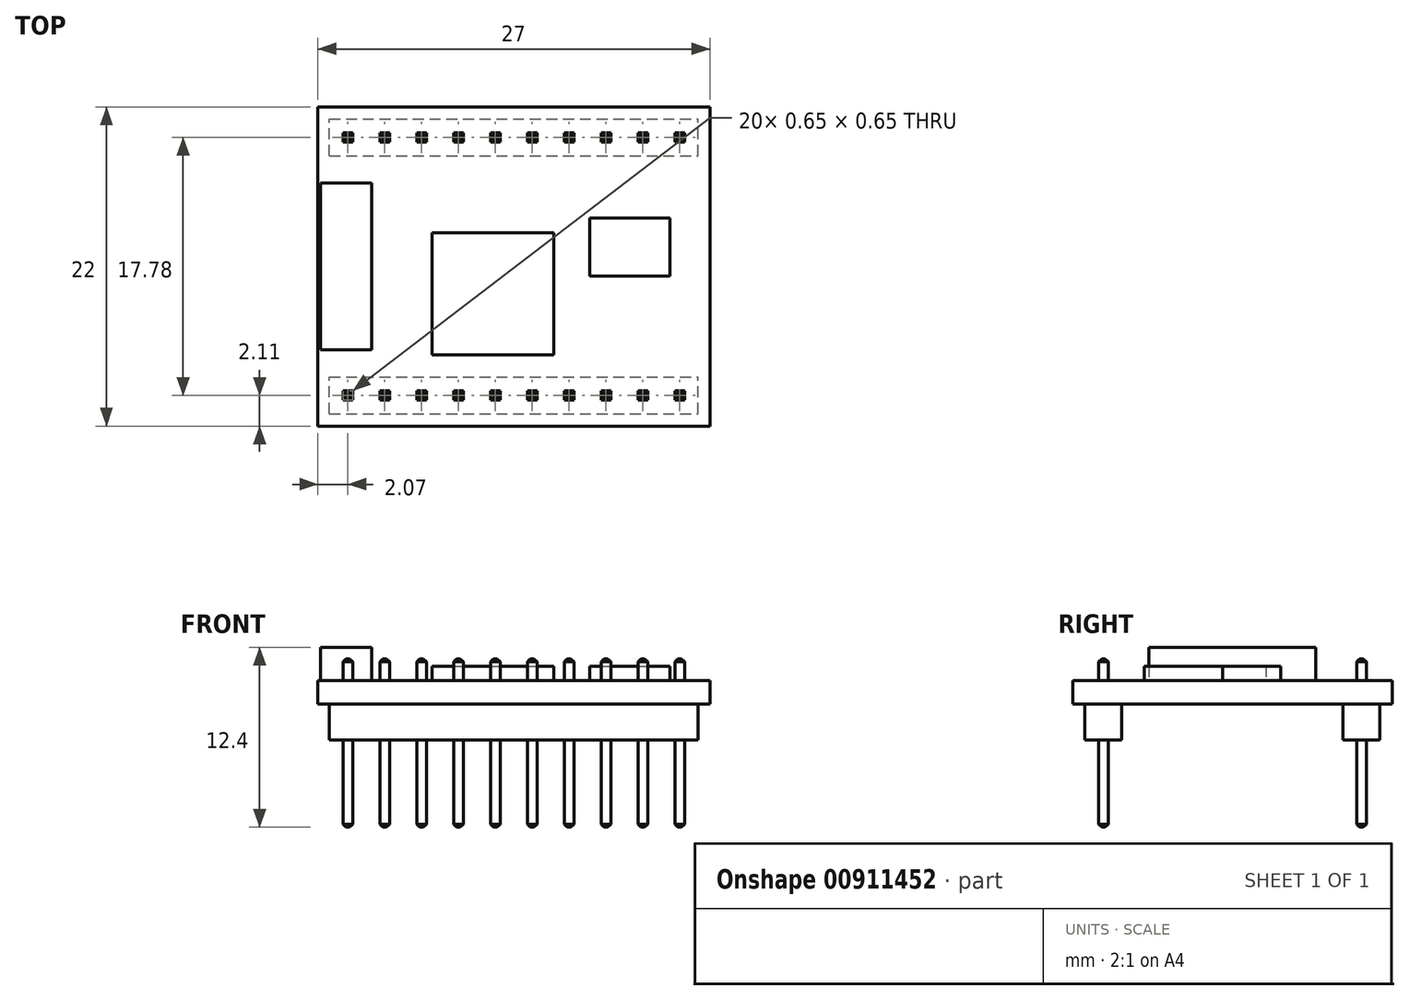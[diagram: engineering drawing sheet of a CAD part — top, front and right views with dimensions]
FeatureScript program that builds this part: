
annotation { "Feature Type Name" : "Feature", "Feature Type Description" : "" }
export const myFeature = defineFeature(function(context is Context, id is Id, definition is map)
    precondition{}
    {
        {
            var Q0;
            Q0=qCreatedBy(makeId("Top.planeOp"),FACE);
            var sketch = newSketch(context, id + "F0", { "sketchPlane" : qUnion([Q0])});
            skLineSegment(sketch, "E0.bottom", {"start": v(-13.5, -11) * mm, "end": v(13.5, -11) * mm});
            skLineSegment(sketch, "E0.top", {"start": v(-13.5, 11) * mm, "end": v(13.5, 11) * mm});
            skLineSegment(sketch, "E0.left", {"start": v(-13.5, -11) * mm, "end": v(-13.5, 11) * mm});
            skLineSegment(sketch, "E0.right", {"start": v(13.5, -11) * mm, "end": v(13.5, 11) * mm});
            skLineSegment(sketch, "E1", {"start": v(-13.5, 11) * mm, "end": v(0, 0) * mm, "construction": true});
            skLineSegment(sketch, "E2", {"start": v(0, 0) * mm, "end": v(-13.5, -11) * mm, "construction": true});
            skLineSegment(sketch, "E3", {"start": v(0, 0) * mm, "end": v(13.5, 11) * mm, "construction": true});
            skSolve(sketch);
        }
        {
            var Q0;
            Q0 = qSketchRegion(id + "F0", true);
            extrude(context, id + "F1", {"entities" : qUnion([Q0]), "depth" : 1.6 * mm, "offsetDistance" : 25 * mm});
        }
        {
            var Q0;
            Q0=makeQuery(id+"F1.opExtrude","CAP_FACE",FACE,{"disambiguationData":[OSD([sQuery(id+"F0.wireOp",EDGE,"E0.bottom"),sQuery(id+"F0.wireOp",EDGE,"E0.top"),sQuery(id+"F0.wireOp",EDGE,"E0.left"),sQuery(id+"F0.wireOp",EDGE,"E0.right")])],"isStart":true});
            var sketch = newSketch(context, id + "F2", { "sketchPlane" : qUnion([Q0])});
            skLineSegment(sketch, "E4.bottom", {"start": v(-12.7, 10.16) * mm, "end": v(12.7, 10.16) * mm});
            skLineSegment(sketch, "E4.top", {"start": v(-12.7, 7.62) * mm, "end": v(12.7, 7.62) * mm});
            skLineSegment(sketch, "E4.left", {"start": v(-12.7, 10.16) * mm, "end": v(-12.7, 7.62) * mm});
            skLineSegment(sketch, "E4.right", {"start": v(12.7, 10.16) * mm, "end": v(12.7, 7.62) * mm});
            skLineSegment(sketch, "E5.bottom", {"start": v(-12.7, -7.62) * mm, "end": v(12.7, -7.62) * mm});
            skLineSegment(sketch, "E5.top", {"start": v(-12.7, -10.16) * mm, "end": v(12.7, -10.16) * mm});
            skLineSegment(sketch, "E5.left", {"start": v(-12.7, -7.62) * mm, "end": v(-12.7, -10.16) * mm});
            skLineSegment(sketch, "E5.right", {"start": v(12.7, -7.62) * mm, "end": v(12.7, -10.16) * mm});
            skLineSegment(sketch, "E6", {"start": v(-13.5, 11) * mm, "end": v(-12.7, 10.16) * mm, "construction": true});
            skLineSegment(sketch, "E7", {"start": v(12.7, 10.16) * mm, "end": v(13.5, 11) * mm, "construction": true});
            skLineSegment(sketch, "E8", {"start": v(-12.7, -10.16) * mm, "end": v(-13.5, -11) * mm, "construction": true});
            skSolve(sketch);
        }
        {
            var Q0;
            Q0 = qSketchRegion(id + "F2", true);
            extrude(context, id + "F3", {"entities" : qUnion([Q0]), "operationType" : NewBodyOperationType.ADD, "depth" : 2.5 * mm, "offsetDistance" : 25 * mm});
        }
        {
            var Q0;
            Q0=makeQuery(id+"F3.opExtrude","CAP_FACE",FACE,{"disambiguationData":[OSD([sQuery(id+"F2.wireOp",EDGE,"E4.bottom"),sQuery(id+"F2.wireOp",EDGE,"E4.top"),sQuery(id+"F2.wireOp",EDGE,"E4.left"),sQuery(id+"F2.wireOp",EDGE,"E4.right")])],"isStart":false});
            var sketch = newSketch(context, id + "F4", { "sketchPlane" : qUnion([Q0])});
            skLineSegment(sketch, "E9.bottom", {"start": v(-11.75, 9.22) * mm, "end": v(-11.1, 9.22) * mm});
            skLineSegment(sketch, "E9.top", {"start": v(-11.75, 8.56) * mm, "end": v(-11.1, 8.56) * mm});
            skLineSegment(sketch, "E9.left", {"start": v(-11.75, 9.22) * mm, "end": v(-11.75, 8.56) * mm});
            skLineSegment(sketch, "E9.right", {"start": v(-11.1, 9.22) * mm, "end": v(-11.1, 8.56) * mm});
            skLineSegment(sketch, "E10.1.0.0", {"start": v(-8.56, 9.22) * mm, "end": v(-8.56, 8.56) * mm});
            skLineSegment(sketch, "E10.1.0.1", {"start": v(-9.21, 8.56) * mm, "end": v(-8.56, 8.56) * mm});
            skLineSegment(sketch, "E10.1.0.2", {"start": v(-9.21, 9.22) * mm, "end": v(-9.21, 8.56) * mm});
            skLineSegment(sketch, "E10.1.0.3", {"start": v(-9.21, 9.22) * mm, "end": v(-8.56, 9.22) * mm});
            skLineSegment(sketch, "E10.2.0.0", {"start": v(-6.02, 9.22) * mm, "end": v(-6.02, 8.56) * mm});
            skLineSegment(sketch, "E10.2.0.1", {"start": v(-6.67, 8.56) * mm, "end": v(-6.02, 8.56) * mm});
            skLineSegment(sketch, "E10.2.0.2", {"start": v(-6.67, 9.22) * mm, "end": v(-6.67, 8.56) * mm});
            skLineSegment(sketch, "E10.2.0.3", {"start": v(-6.67, 9.22) * mm, "end": v(-6.02, 9.22) * mm});
            skLineSegment(sketch, "E10.3.0.0", {"start": v(-3.48, 9.22) * mm, "end": v(-3.48, 8.56) * mm});
            skLineSegment(sketch, "E10.3.0.1", {"start": v(-4.13, 8.56) * mm, "end": v(-3.48, 8.56) * mm});
            skLineSegment(sketch, "E10.3.0.2", {"start": v(-4.13, 9.22) * mm, "end": v(-4.13, 8.56) * mm});
            skLineSegment(sketch, "E10.3.0.3", {"start": v(-4.13, 9.22) * mm, "end": v(-3.48, 9.22) * mm});
            skLineSegment(sketch, "E10.4.0.0", {"start": v(-0.94, 9.22) * mm, "end": v(-0.94, 8.56) * mm});
            skLineSegment(sketch, "E10.4.0.1", {"start": v(-1.6, 8.56) * mm, "end": v(-0.94, 8.56) * mm});
            skLineSegment(sketch, "E10.4.0.2", {"start": v(-1.6, 9.22) * mm, "end": v(-1.6, 8.56) * mm});
            skLineSegment(sketch, "E10.4.0.3", {"start": v(-1.6, 9.22) * mm, "end": v(-0.94, 9.22) * mm});
            skLineSegment(sketch, "E10.5.0.0", {"start": v(1.6, 9.22) * mm, "end": v(1.6, 8.56) * mm});
            skLineSegment(sketch, "E10.5.0.1", {"start": v(0.95, 8.56) * mm, "end": v(1.6, 8.56) * mm});
            skLineSegment(sketch, "E10.5.0.2", {"start": v(0.95, 9.22) * mm, "end": v(0.95, 8.56) * mm});
            skLineSegment(sketch, "E10.5.0.3", {"start": v(0.95, 9.22) * mm, "end": v(1.6, 9.22) * mm});
            skLineSegment(sketch, "E10.6.0.0", {"start": v(4.14, 9.22) * mm, "end": v(4.14, 8.56) * mm});
            skLineSegment(sketch, "E10.6.0.1", {"start": v(3.49, 8.56) * mm, "end": v(4.14, 8.56) * mm});
            skLineSegment(sketch, "E10.6.0.2", {"start": v(3.49, 9.22) * mm, "end": v(3.49, 8.56) * mm});
            skLineSegment(sketch, "E10.6.0.3", {"start": v(3.49, 9.22) * mm, "end": v(4.14, 9.22) * mm});
            skLineSegment(sketch, "E10.7.0.0", {"start": v(6.68, 9.22) * mm, "end": v(6.68, 8.56) * mm});
            skLineSegment(sketch, "E10.7.0.1", {"start": v(6.03, 8.56) * mm, "end": v(6.68, 8.56) * mm});
            skLineSegment(sketch, "E10.7.0.2", {"start": v(6.03, 9.22) * mm, "end": v(6.03, 8.56) * mm});
            skLineSegment(sketch, "E10.7.0.3", {"start": v(6.03, 9.22) * mm, "end": v(6.68, 9.22) * mm});
            skLineSegment(sketch, "E10.8.0.0", {"start": v(9.22, 9.22) * mm, "end": v(9.22, 8.56) * mm});
            skLineSegment(sketch, "E10.8.0.1", {"start": v(8.57, 8.56) * mm, "end": v(9.22, 8.56) * mm});
            skLineSegment(sketch, "E10.8.0.2", {"start": v(8.57, 9.22) * mm, "end": v(8.57, 8.56) * mm});
            skLineSegment(sketch, "E10.8.0.3", {"start": v(8.57, 9.22) * mm, "end": v(9.22, 9.22) * mm});
            skLineSegment(sketch, "E10.9.0.0", {"start": v(11.76, 9.22) * mm, "end": v(11.76, 8.56) * mm});
            skLineSegment(sketch, "E10.9.0.1", {"start": v(11.1, 8.56) * mm, "end": v(11.76, 8.56) * mm});
            skLineSegment(sketch, "E10.9.0.2", {"start": v(11.1, 9.22) * mm, "end": v(11.1, 8.56) * mm});
            skLineSegment(sketch, "E10.9.0.3", {"start": v(11.1, 9.22) * mm, "end": v(11.76, 9.22) * mm});
            skLineSegment(sketch, "E10.direction1", {"start": v(-11.75, 8.56) * mm, "end": v(-9.21, 8.56) * mm, "construction": true});
            skLineSegment(sketch, "E11", {"start": v(-12.7, 10.16) * mm, "end": v(-11.76, 9.22) * mm, "construction": true});
            skLineSegment(sketch, "E12", {"start": v(-11.75, 8.56) * mm, "end": v(-12.7, 7.62) * mm, "construction": true});
            skLineSegment(sketch, "E13", {"start": v(11.76, 9.22) * mm, "end": v(12.7, 10.16) * mm, "construction": true});
            skLineSegment(sketch, "E14", {"start": v(0, 0) * mm, "end": v(16.19, 0) * mm, "construction": true});
            skLineSegment(sketch, "E15.MirrorCS", {"start": v(6.03, -8.56) * mm, "end": v(6.68, -8.56) * mm});
            skLineSegment(sketch, "E16.MirrorCS", {"start": v(3.49, -9.22) * mm, "end": v(3.49, -8.56) * mm});
            skLineSegment(sketch, "E17.MirrorCS", {"start": v(-0.94, -9.22) * mm, "end": v(-0.94, -8.56) * mm});
            skLineSegment(sketch, "E18.MirrorCS", {"start": v(-1.6, -9.22) * mm, "end": v(-1.6, -8.56) * mm});
            skLineSegment(sketch, "E19.MirrorCS", {"start": v(-6.67, -9.22) * mm, "end": v(-6.02, -9.22) * mm});
            skLineSegment(sketch, "E20.MirrorCS", {"start": v(11.76, -9.22) * mm, "end": v(11.76, -8.56) * mm});
            skLineSegment(sketch, "E21.MirrorCS", {"start": v(-4.13, -9.22) * mm, "end": v(-4.13, -8.56) * mm});
            skLineSegment(sketch, "E22.MirrorCS", {"start": v(11.1, -9.22) * mm, "end": v(11.76, -9.22) * mm});
            skLineSegment(sketch, "E23.MirrorCS", {"start": v(8.57, -9.22) * mm, "end": v(8.57, -8.56) * mm});
            skLineSegment(sketch, "E24.MirrorCS", {"start": v(0.95, -9.22) * mm, "end": v(0.95, -8.56) * mm});
            skLineSegment(sketch, "E25.MirrorCS", {"start": v(1.6, -9.22) * mm, "end": v(1.6, -8.56) * mm});
            skLineSegment(sketch, "E26.MirrorCS", {"start": v(8.57, -8.56) * mm, "end": v(9.22, -8.56) * mm});
            skLineSegment(sketch, "E27.MirrorCS", {"start": v(11.1, -8.56) * mm, "end": v(11.76, -8.56) * mm});
            skLineSegment(sketch, "E28.MirrorCS", {"start": v(3.49, -8.56) * mm, "end": v(4.14, -8.56) * mm});
            skLineSegment(sketch, "E29.MirrorCS", {"start": v(6.68, -9.22) * mm, "end": v(6.68, -8.56) * mm});
            skLineSegment(sketch, "E30.MirrorCS", {"start": v(-1.6, -9.22) * mm, "end": v(-0.94, -9.22) * mm});
            skLineSegment(sketch, "E31.MirrorCS", {"start": v(6.03, -9.22) * mm, "end": v(6.68, -9.22) * mm});
            skLineSegment(sketch, "E32.MirrorCS", {"start": v(6.03, -9.22) * mm, "end": v(6.03, -8.56) * mm});
            skLineSegment(sketch, "E33.MirrorCS", {"start": v(11.1, -9.22) * mm, "end": v(11.1, -8.56) * mm});
            skLineSegment(sketch, "E34.MirrorCS", {"start": v(0.95, -9.22) * mm, "end": v(1.6, -9.22) * mm});
            skLineSegment(sketch, "E35.MirrorCS", {"start": v(4.14, -9.22) * mm, "end": v(4.14, -8.56) * mm});
            skLineSegment(sketch, "E36.MirrorCS", {"start": v(-4.13, -9.22) * mm, "end": v(-3.48, -9.22) * mm});
            skLineSegment(sketch, "E37.MirrorCS", {"start": v(-4.13, -8.56) * mm, "end": v(-3.48, -8.56) * mm});
            skLineSegment(sketch, "E38.MirrorCS", {"start": v(-6.67, -9.22) * mm, "end": v(-6.67, -8.56) * mm});
            skLineSegment(sketch, "E39.MirrorCS", {"start": v(8.57, -9.22) * mm, "end": v(9.22, -9.22) * mm});
            skLineSegment(sketch, "E40.MirrorCS", {"start": v(0.95, -8.56) * mm, "end": v(1.6, -8.56) * mm});
            skLineSegment(sketch, "E41.MirrorCS", {"start": v(-3.48, -9.22) * mm, "end": v(-3.48, -8.56) * mm});
            skLineSegment(sketch, "E42.MirrorCS", {"start": v(-6.67, -8.56) * mm, "end": v(-6.02, -8.56) * mm});
            skLineSegment(sketch, "E43.MirrorCS", {"start": v(-6.02, -9.22) * mm, "end": v(-6.02, -8.56) * mm});
            skLineSegment(sketch, "E44.MirrorCS", {"start": v(-1.6, -8.56) * mm, "end": v(-0.94, -8.56) * mm});
            skLineSegment(sketch, "E45.MirrorCS", {"start": v(9.22, -9.22) * mm, "end": v(9.22, -8.56) * mm});
            skLineSegment(sketch, "E46.MirrorCS", {"start": v(3.49, -9.22) * mm, "end": v(4.14, -9.22) * mm});
            skLineSegment(sketch, "E47.MirrorCS", {"start": v(-9.21, -9.22) * mm, "end": v(-9.21, -8.56) * mm});
            skLineSegment(sketch, "E48.MirrorCS", {"start": v(-9.21, -9.22) * mm, "end": v(-8.56, -9.22) * mm});
            skLineSegment(sketch, "E49.MirrorCS", {"start": v(-9.21, -8.56) * mm, "end": v(-8.56, -8.56) * mm});
            skLineSegment(sketch, "E50.MirrorCS", {"start": v(-8.56, -9.22) * mm, "end": v(-8.56, -8.56) * mm});
            skLineSegment(sketch, "E51.MirrorCS", {"start": v(-11.75, -8.56) * mm, "end": v(-11.1, -8.56) * mm});
            skLineSegment(sketch, "E52.MirrorCS", {"start": v(-11.75, -9.22) * mm, "end": v(-11.75, -8.56) * mm});
            skLineSegment(sketch, "E53.MirrorCS", {"start": v(-11.1, -9.22) * mm, "end": v(-11.1, -8.56) * mm});
            skLineSegment(sketch, "E54.MirrorCS", {"start": v(-11.75, -9.22) * mm, "end": v(-11.1, -9.22) * mm});
            skSolve(sketch);
        }
        {
            var Q0;
            Q0 = qSketchRegion(id + "F4", true);
            extrude(context, id + "F5", {"entities" : qUnion([Q0]), "operationType" : NewBodyOperationType.ADD, "depth" : 6 * mm, "offsetDistance" : 25 * mm});
        }
        {
            var Q0;
            Q0=makeQuery(id+"F1.opExtrude","CAP_FACE",FACE,{"disambiguationData":[OSD([sQuery(id+"F0.wireOp",EDGE,"E0.bottom"),sQuery(id+"F0.wireOp",EDGE,"E0.top"),sQuery(id+"F0.wireOp",EDGE,"E0.left"),sQuery(id+"F0.wireOp",EDGE,"E0.right")])],"isStart":false});
            var sketch = newSketch(context, id + "F6", { "sketchPlane" : qUnion([Q0])});
            skLineSegment(sketch, "E55.0.0", {"start": v(-11.75, 8.56) * mm, "end": v(-11.75, 9.22) * mm});
            skLineSegment(sketch, "E55.0.1", {"start": v(-11.75, 9.22) * mm, "end": v(-11.1, 9.22) * mm});
            skLineSegment(sketch, "E55.0.2", {"start": v(-11.1, 9.22) * mm, "end": v(-11.1, 8.56) * mm});
            skLineSegment(sketch, "E55.0.3", {"start": v(-11.1, 8.56) * mm, "end": v(-11.75, 8.56) * mm});
            skLineSegment(sketch, "E56.0.0", {"start": v(-9.21, 9.22) * mm, "end": v(-8.56, 9.22) * mm});
            skLineSegment(sketch, "E56.0.1", {"start": v(-8.56, 9.22) * mm, "end": v(-8.56, 8.56) * mm});
            skLineSegment(sketch, "E56.0.2", {"start": v(-8.56, 8.56) * mm, "end": v(-9.21, 8.56) * mm});
            skLineSegment(sketch, "E56.0.3", {"start": v(-9.21, 8.56) * mm, "end": v(-9.21, 9.22) * mm});
            skLineSegment(sketch, "E57.0.0", {"start": v(-6.67, 9.22) * mm, "end": v(-6.02, 9.22) * mm});
            skLineSegment(sketch, "E57.0.1", {"start": v(-6.02, 9.22) * mm, "end": v(-6.02, 8.56) * mm});
            skLineSegment(sketch, "E57.0.2", {"start": v(-6.02, 8.56) * mm, "end": v(-6.67, 8.56) * mm});
            skLineSegment(sketch, "E57.0.3", {"start": v(-6.67, 8.56) * mm, "end": v(-6.67, 9.22) * mm});
            skLineSegment(sketch, "E58.0.0", {"start": v(-4.13, 9.22) * mm, "end": v(-3.48, 9.22) * mm});
            skLineSegment(sketch, "E58.0.1", {"start": v(-3.48, 9.22) * mm, "end": v(-3.48, 8.56) * mm});
            skLineSegment(sketch, "E58.0.2", {"start": v(-3.48, 8.56) * mm, "end": v(-4.13, 8.56) * mm});
            skLineSegment(sketch, "E58.0.3", {"start": v(-4.13, 8.56) * mm, "end": v(-4.13, 9.22) * mm});
            skLineSegment(sketch, "E59.0.0", {"start": v(-1.6, 8.56) * mm, "end": v(-1.6, 9.22) * mm});
            skLineSegment(sketch, "E59.0.1", {"start": v(-1.6, 9.22) * mm, "end": v(-0.94, 9.22) * mm});
            skLineSegment(sketch, "E59.0.2", {"start": v(-0.94, 9.22) * mm, "end": v(-0.94, 8.56) * mm});
            skLineSegment(sketch, "E59.0.3", {"start": v(-0.94, 8.56) * mm, "end": v(-1.6, 8.56) * mm});
            skLineSegment(sketch, "E60.0.0", {"start": v(0.95, 9.22) * mm, "end": v(1.6, 9.22) * mm});
            skLineSegment(sketch, "E60.0.1", {"start": v(1.6, 9.22) * mm, "end": v(1.6, 8.56) * mm});
            skLineSegment(sketch, "E60.0.2", {"start": v(1.6, 8.56) * mm, "end": v(0.95, 8.56) * mm});
            skLineSegment(sketch, "E60.0.3", {"start": v(0.95, 8.56) * mm, "end": v(0.95, 9.22) * mm});
            skLineSegment(sketch, "E61.0.0", {"start": v(3.49, 8.56) * mm, "end": v(3.49, 9.22) * mm});
            skLineSegment(sketch, "E61.0.1", {"start": v(3.49, 9.22) * mm, "end": v(4.14, 9.22) * mm});
            skLineSegment(sketch, "E61.0.2", {"start": v(4.14, 9.22) * mm, "end": v(4.14, 8.56) * mm});
            skLineSegment(sketch, "E61.0.3", {"start": v(4.14, 8.56) * mm, "end": v(3.49, 8.56) * mm});
            skLineSegment(sketch, "E62.0.0", {"start": v(6.03, 8.56) * mm, "end": v(6.03, 9.22) * mm});
            skLineSegment(sketch, "E62.0.1", {"start": v(6.03, 9.22) * mm, "end": v(6.68, 9.22) * mm});
            skLineSegment(sketch, "E62.0.2", {"start": v(6.68, 9.22) * mm, "end": v(6.68, 8.56) * mm});
            skLineSegment(sketch, "E62.0.3", {"start": v(6.68, 8.56) * mm, "end": v(6.03, 8.56) * mm});
            skLineSegment(sketch, "E63.0.0", {"start": v(8.57, 9.22) * mm, "end": v(9.22, 9.22) * mm});
            skLineSegment(sketch, "E63.0.1", {"start": v(9.22, 9.22) * mm, "end": v(9.22, 8.56) * mm});
            skLineSegment(sketch, "E63.0.2", {"start": v(9.22, 8.56) * mm, "end": v(8.57, 8.56) * mm});
            skLineSegment(sketch, "E63.0.3", {"start": v(8.57, 8.56) * mm, "end": v(8.57, 9.22) * mm});
            skLineSegment(sketch, "E64.0.0", {"start": v(11.1, 8.56) * mm, "end": v(11.1, 9.22) * mm});
            skLineSegment(sketch, "E64.0.1", {"start": v(11.1, 9.22) * mm, "end": v(11.76, 9.22) * mm});
            skLineSegment(sketch, "E64.0.2", {"start": v(11.76, 9.22) * mm, "end": v(11.76, 8.56) * mm});
            skLineSegment(sketch, "E64.0.3", {"start": v(11.76, 8.56) * mm, "end": v(11.1, 8.56) * mm});
            skLineSegment(sketch, "E65.0.0", {"start": v(-11.75, -9.22) * mm, "end": v(-11.75, -8.56) * mm});
            skLineSegment(sketch, "E65.0.1", {"start": v(-11.75, -8.56) * mm, "end": v(-11.1, -8.56) * mm});
            skLineSegment(sketch, "E65.0.2", {"start": v(-11.1, -8.56) * mm, "end": v(-11.1, -9.22) * mm});
            skLineSegment(sketch, "E65.0.3", {"start": v(-11.1, -9.22) * mm, "end": v(-11.75, -9.22) * mm});
            skLineSegment(sketch, "E66.0.0", {"start": v(-8.56, -9.22) * mm, "end": v(-9.21, -9.22) * mm});
            skLineSegment(sketch, "E66.0.1", {"start": v(-9.21, -9.22) * mm, "end": v(-9.21, -8.56) * mm});
            skLineSegment(sketch, "E66.0.2", {"start": v(-9.21, -8.56) * mm, "end": v(-8.56, -8.56) * mm});
            skLineSegment(sketch, "E66.0.3", {"start": v(-8.56, -8.56) * mm, "end": v(-8.56, -9.22) * mm});
            skLineSegment(sketch, "E67.0.0", {"start": v(-6.02, -9.22) * mm, "end": v(-6.67, -9.22) * mm});
            skLineSegment(sketch, "E67.0.1", {"start": v(-6.67, -9.22) * mm, "end": v(-6.67, -8.56) * mm});
            skLineSegment(sketch, "E67.0.2", {"start": v(-6.67, -8.56) * mm, "end": v(-6.02, -8.56) * mm});
            skLineSegment(sketch, "E67.0.3", {"start": v(-6.02, -8.56) * mm, "end": v(-6.02, -9.22) * mm});
            skLineSegment(sketch, "E68.0.0", {"start": v(-3.48, -9.22) * mm, "end": v(-4.13, -9.22) * mm});
            skLineSegment(sketch, "E68.0.1", {"start": v(-4.13, -9.22) * mm, "end": v(-4.13, -8.56) * mm});
            skLineSegment(sketch, "E68.0.2", {"start": v(-4.13, -8.56) * mm, "end": v(-3.48, -8.56) * mm});
            skLineSegment(sketch, "E68.0.3", {"start": v(-3.48, -8.56) * mm, "end": v(-3.48, -9.22) * mm});
            skLineSegment(sketch, "E69.0.0", {"start": v(-0.94, -9.22) * mm, "end": v(-1.6, -9.22) * mm});
            skLineSegment(sketch, "E69.0.1", {"start": v(-1.6, -9.22) * mm, "end": v(-1.6, -8.56) * mm});
            skLineSegment(sketch, "E69.0.2", {"start": v(-1.6, -8.56) * mm, "end": v(-0.94, -8.56) * mm});
            skLineSegment(sketch, "E69.0.3", {"start": v(-0.94, -8.56) * mm, "end": v(-0.94, -9.22) * mm});
            skLineSegment(sketch, "E70.0.0", {"start": v(1.6, -9.22) * mm, "end": v(0.95, -9.22) * mm});
            skLineSegment(sketch, "E70.0.1", {"start": v(0.95, -9.22) * mm, "end": v(0.95, -8.56) * mm});
            skLineSegment(sketch, "E70.0.2", {"start": v(0.95, -8.56) * mm, "end": v(1.6, -8.56) * mm});
            skLineSegment(sketch, "E70.0.3", {"start": v(1.6, -8.56) * mm, "end": v(1.6, -9.22) * mm});
            skLineSegment(sketch, "E71.0.0", {"start": v(4.14, -9.22) * mm, "end": v(3.49, -9.22) * mm});
            skLineSegment(sketch, "E71.0.1", {"start": v(3.49, -9.22) * mm, "end": v(3.49, -8.56) * mm});
            skLineSegment(sketch, "E71.0.2", {"start": v(3.49, -8.56) * mm, "end": v(4.14, -8.56) * mm});
            skLineSegment(sketch, "E71.0.3", {"start": v(4.14, -8.56) * mm, "end": v(4.14, -9.22) * mm});
            skLineSegment(sketch, "E72.0.0", {"start": v(6.68, -9.22) * mm, "end": v(6.03, -9.22) * mm});
            skLineSegment(sketch, "E72.0.1", {"start": v(6.03, -9.22) * mm, "end": v(6.03, -8.56) * mm});
            skLineSegment(sketch, "E72.0.2", {"start": v(6.03, -8.56) * mm, "end": v(6.68, -8.56) * mm});
            skLineSegment(sketch, "E72.0.3", {"start": v(6.68, -8.56) * mm, "end": v(6.68, -9.22) * mm});
            skLineSegment(sketch, "E73.0.0", {"start": v(9.22, -9.22) * mm, "end": v(8.57, -9.22) * mm});
            skLineSegment(sketch, "E73.0.1", {"start": v(8.57, -9.22) * mm, "end": v(8.57, -8.56) * mm});
            skLineSegment(sketch, "E73.0.2", {"start": v(8.57, -8.56) * mm, "end": v(9.22, -8.56) * mm});
            skLineSegment(sketch, "E73.0.3", {"start": v(9.22, -8.56) * mm, "end": v(9.22, -9.22) * mm});
            skLineSegment(sketch, "E74.0.0", {"start": v(11.76, -9.22) * mm, "end": v(11.1, -9.22) * mm});
            skLineSegment(sketch, "E74.0.1", {"start": v(11.1, -9.22) * mm, "end": v(11.1, -8.56) * mm});
            skLineSegment(sketch, "E74.0.2", {"start": v(11.1, -8.56) * mm, "end": v(11.76, -8.56) * mm});
            skLineSegment(sketch, "E74.0.3", {"start": v(11.76, -8.56) * mm, "end": v(11.76, -9.22) * mm});
            skSolve(sketch);
        }
        {
            var Q0;
            Q0 = qSketchRegion(id + "F6", true);
            extrude(context, id + "F7", {"entities" : qUnion([Q0]), "operationType" : NewBodyOperationType.ADD, "depth" : 1.5 * mm, "offsetDistance" : 25 * mm});
        }
        {
            var Q0;
            Q0=makeQuery(id+"F5.opExtrude","CAP_FACE",FACE,{"disambiguationData":[OSD([sQuery(id+"F4.wireOp",EDGE,"E9.bottom"),sQuery(id+"F4.wireOp",EDGE,"E9.top"),sQuery(id+"F4.wireOp",EDGE,"E9.left"),sQuery(id+"F4.wireOp",EDGE,"E9.right")])],"isStart":false});
            var Q1;
            Q1=makeQuery(id+"F5.opExtrude","CAP_FACE",FACE,{"disambiguationData":[OSD([sQuery(id+"F4.wireOp",EDGE,"E10.1.0.0"),sQuery(id+"F4.wireOp",EDGE,"E10.1.0.1"),sQuery(id+"F4.wireOp",EDGE,"E10.1.0.2"),sQuery(id+"F4.wireOp",EDGE,"E10.1.0.3")])],"isStart":false});
            var Q2;
            Q2=makeQuery(id+"F5.opExtrude","CAP_FACE",FACE,{"disambiguationData":[OSD([sQuery(id+"F4.wireOp",EDGE,"E10.2.0.0"),sQuery(id+"F4.wireOp",EDGE,"E10.2.0.1"),sQuery(id+"F4.wireOp",EDGE,"E10.2.0.2"),sQuery(id+"F4.wireOp",EDGE,"E10.2.0.3")])],"isStart":false});
            var Q3;
            Q3=makeQuery(id+"F5.opExtrude","CAP_FACE",FACE,{"disambiguationData":[OSD([sQuery(id+"F4.wireOp",EDGE,"E10.3.0.0"),sQuery(id+"F4.wireOp",EDGE,"E10.3.0.1"),sQuery(id+"F4.wireOp",EDGE,"E10.3.0.2"),sQuery(id+"F4.wireOp",EDGE,"E10.3.0.3")])],"isStart":false});
            var Q4;
            Q4=makeQuery(id+"F5.opExtrude","CAP_FACE",FACE,{"disambiguationData":[OSD([sQuery(id+"F4.wireOp",EDGE,"E10.4.0.0"),sQuery(id+"F4.wireOp",EDGE,"E10.4.0.1"),sQuery(id+"F4.wireOp",EDGE,"E10.4.0.2"),sQuery(id+"F4.wireOp",EDGE,"E10.4.0.3")])],"isStart":false});
            var Q5;
            Q5=makeQuery(id+"F5.opExtrude","CAP_FACE",FACE,{"disambiguationData":[OSD([sQuery(id+"F4.wireOp",EDGE,"E10.5.0.0"),sQuery(id+"F4.wireOp",EDGE,"E10.5.0.1"),sQuery(id+"F4.wireOp",EDGE,"E10.5.0.2"),sQuery(id+"F4.wireOp",EDGE,"E10.5.0.3")])],"isStart":false});
            var Q6;
            Q6=makeQuery(id+"F5.opExtrude","CAP_FACE",FACE,{"disambiguationData":[OSD([sQuery(id+"F4.wireOp",EDGE,"E10.6.0.0"),sQuery(id+"F4.wireOp",EDGE,"E10.6.0.1"),sQuery(id+"F4.wireOp",EDGE,"E10.6.0.2"),sQuery(id+"F4.wireOp",EDGE,"E10.6.0.3")])],"isStart":false});
            var Q7;
            Q7=makeQuery(id+"F5.opExtrude","CAP_FACE",FACE,{"disambiguationData":[OSD([sQuery(id+"F4.wireOp",EDGE,"E10.7.0.0"),sQuery(id+"F4.wireOp",EDGE,"E10.7.0.1"),sQuery(id+"F4.wireOp",EDGE,"E10.7.0.2"),sQuery(id+"F4.wireOp",EDGE,"E10.7.0.3")])],"isStart":false});
            var Q8;
            Q8=makeQuery(id+"F5.opExtrude","CAP_FACE",FACE,{"disambiguationData":[OSD([sQuery(id+"F4.wireOp",EDGE,"E10.8.0.0"),sQuery(id+"F4.wireOp",EDGE,"E10.8.0.1"),sQuery(id+"F4.wireOp",EDGE,"E10.8.0.2"),sQuery(id+"F4.wireOp",EDGE,"E10.8.0.3")])],"isStart":false});
            var Q9;
            Q9=makeQuery(id+"F5.opExtrude","CAP_FACE",FACE,{"disambiguationData":[OSD([sQuery(id+"F4.wireOp",EDGE,"E10.9.0.0"),sQuery(id+"F4.wireOp",EDGE,"E10.9.0.1"),sQuery(id+"F4.wireOp",EDGE,"E10.9.0.2"),sQuery(id+"F4.wireOp",EDGE,"E10.9.0.3")])],"isStart":false});
            var Q10;
            Q10=makeQuery(id+"F5.opExtrude","CAP_FACE",FACE,{"disambiguationData":[OSD([sQuery(id+"F4.wireOp",EDGE,"E51.MirrorCS"),sQuery(id+"F4.wireOp",EDGE,"E52.MirrorCS"),sQuery(id+"F4.wireOp",EDGE,"E53.MirrorCS"),sQuery(id+"F4.wireOp",EDGE,"E54.MirrorCS")])],"isStart":false});
            var Q11;
            Q11=makeQuery(id+"F5.opExtrude","CAP_FACE",FACE,{"disambiguationData":[OSD([sQuery(id+"F4.wireOp",EDGE,"E47.MirrorCS"),sQuery(id+"F4.wireOp",EDGE,"E48.MirrorCS"),sQuery(id+"F4.wireOp",EDGE,"E49.MirrorCS"),sQuery(id+"F4.wireOp",EDGE,"E50.MirrorCS")])],"isStart":false});
            var Q12;
            Q12=makeQuery(id+"F5.opExtrude","CAP_FACE",FACE,{"disambiguationData":[OSD([sQuery(id+"F4.wireOp",EDGE,"E19.MirrorCS"),sQuery(id+"F4.wireOp",EDGE,"E38.MirrorCS"),sQuery(id+"F4.wireOp",EDGE,"E42.MirrorCS"),sQuery(id+"F4.wireOp",EDGE,"E43.MirrorCS")])],"isStart":false});
            var Q13;
            Q13=makeQuery(id+"F5.opExtrude","CAP_FACE",FACE,{"disambiguationData":[OSD([sQuery(id+"F4.wireOp",EDGE,"E21.MirrorCS"),sQuery(id+"F4.wireOp",EDGE,"E36.MirrorCS"),sQuery(id+"F4.wireOp",EDGE,"E37.MirrorCS"),sQuery(id+"F4.wireOp",EDGE,"E41.MirrorCS")])],"isStart":false});
            var Q14;
            Q14=makeQuery(id+"F5.opExtrude","CAP_FACE",FACE,{"disambiguationData":[OSD([sQuery(id+"F4.wireOp",EDGE,"E17.MirrorCS"),sQuery(id+"F4.wireOp",EDGE,"E18.MirrorCS"),sQuery(id+"F4.wireOp",EDGE,"E30.MirrorCS"),sQuery(id+"F4.wireOp",EDGE,"E44.MirrorCS")])],"isStart":false});
            var Q15;
            Q15=makeQuery(id+"F5.opExtrude","CAP_FACE",FACE,{"disambiguationData":[OSD([sQuery(id+"F4.wireOp",EDGE,"E24.MirrorCS"),sQuery(id+"F4.wireOp",EDGE,"E25.MirrorCS"),sQuery(id+"F4.wireOp",EDGE,"E34.MirrorCS"),sQuery(id+"F4.wireOp",EDGE,"E40.MirrorCS")])],"isStart":false});
            var Q16;
            Q16=makeQuery(id+"F5.opExtrude","CAP_FACE",FACE,{"disambiguationData":[OSD([sQuery(id+"F4.wireOp",EDGE,"E16.MirrorCS"),sQuery(id+"F4.wireOp",EDGE,"E28.MirrorCS"),sQuery(id+"F4.wireOp",EDGE,"E35.MirrorCS"),sQuery(id+"F4.wireOp",EDGE,"E46.MirrorCS")])],"isStart":false});
            var Q17;
            Q17=makeQuery(id+"F5.opExtrude","CAP_FACE",FACE,{"disambiguationData":[OSD([sQuery(id+"F4.wireOp",EDGE,"E15.MirrorCS"),sQuery(id+"F4.wireOp",EDGE,"E29.MirrorCS"),sQuery(id+"F4.wireOp",EDGE,"E31.MirrorCS"),sQuery(id+"F4.wireOp",EDGE,"E32.MirrorCS")])],"isStart":false});
            var Q18;
            Q18=makeQuery(id+"F5.opExtrude","CAP_FACE",FACE,{"disambiguationData":[OSD([sQuery(id+"F4.wireOp",EDGE,"E23.MirrorCS"),sQuery(id+"F4.wireOp",EDGE,"E26.MirrorCS"),sQuery(id+"F4.wireOp",EDGE,"E39.MirrorCS"),sQuery(id+"F4.wireOp",EDGE,"E45.MirrorCS")])],"isStart":false});
            var Q19;
            Q19=makeQuery(id+"F5.opExtrude","CAP_FACE",FACE,{"disambiguationData":[OSD([sQuery(id+"F4.wireOp",EDGE,"E20.MirrorCS"),sQuery(id+"F4.wireOp",EDGE,"E22.MirrorCS"),sQuery(id+"F4.wireOp",EDGE,"E27.MirrorCS"),sQuery(id+"F4.wireOp",EDGE,"E33.MirrorCS")])],"isStart":false});
            var Q20;
            Q20=makeQuery(id+"F7.opExtrude","CAP_FACE",FACE,{"disambiguationData":[OSD([sQuery(id+"F6.wireOp",EDGE,"E55.0.0"),sQuery(id+"F6.wireOp",EDGE,"E55.0.1"),sQuery(id+"F6.wireOp",EDGE,"E55.0.2"),sQuery(id+"F6.wireOp",EDGE,"E55.0.3")])],"isStart":false});
            var Q21;
            Q21=makeQuery(id+"F7.opExtrude","CAP_FACE",FACE,{"disambiguationData":[OSD([sQuery(id+"F6.wireOp",EDGE,"E56.0.0"),sQuery(id+"F6.wireOp",EDGE,"E56.0.1"),sQuery(id+"F6.wireOp",EDGE,"E56.0.2"),sQuery(id+"F6.wireOp",EDGE,"E56.0.3")])],"isStart":false});
            var Q22;
            Q22=makeQuery(id+"F7.opExtrude","CAP_FACE",FACE,{"disambiguationData":[OSD([sQuery(id+"F6.wireOp",EDGE,"E57.0.0"),sQuery(id+"F6.wireOp",EDGE,"E57.0.1"),sQuery(id+"F6.wireOp",EDGE,"E57.0.2"),sQuery(id+"F6.wireOp",EDGE,"E57.0.3")])],"isStart":false});
            var Q23;
            Q23=makeQuery(id+"F7.opExtrude","CAP_FACE",FACE,{"disambiguationData":[OSD([sQuery(id+"F6.wireOp",EDGE,"E58.0.0"),sQuery(id+"F6.wireOp",EDGE,"E58.0.1"),sQuery(id+"F6.wireOp",EDGE,"E58.0.2"),sQuery(id+"F6.wireOp",EDGE,"E58.0.3")])],"isStart":false});
            var Q24;
            Q24=makeQuery(id+"F7.opExtrude","CAP_FACE",FACE,{"disambiguationData":[OSD([sQuery(id+"F6.wireOp",EDGE,"E59.0.0"),sQuery(id+"F6.wireOp",EDGE,"E59.0.1"),sQuery(id+"F6.wireOp",EDGE,"E59.0.2"),sQuery(id+"F6.wireOp",EDGE,"E59.0.3")])],"isStart":false});
            var Q25;
            Q25=makeQuery(id+"F7.opExtrude","CAP_FACE",FACE,{"disambiguationData":[OSD([sQuery(id+"F6.wireOp",EDGE,"E60.0.0"),sQuery(id+"F6.wireOp",EDGE,"E60.0.1"),sQuery(id+"F6.wireOp",EDGE,"E60.0.2"),sQuery(id+"F6.wireOp",EDGE,"E60.0.3")])],"isStart":false});
            var Q26;
            Q26=makeQuery(id+"F7.opExtrude","CAP_FACE",FACE,{"disambiguationData":[OSD([sQuery(id+"F6.wireOp",EDGE,"E61.0.0"),sQuery(id+"F6.wireOp",EDGE,"E61.0.1"),sQuery(id+"F6.wireOp",EDGE,"E61.0.2"),sQuery(id+"F6.wireOp",EDGE,"E61.0.3")])],"isStart":false});
            var Q27;
            Q27=makeQuery(id+"F7.opExtrude","CAP_FACE",FACE,{"disambiguationData":[OSD([sQuery(id+"F6.wireOp",EDGE,"E62.0.0"),sQuery(id+"F6.wireOp",EDGE,"E62.0.1"),sQuery(id+"F6.wireOp",EDGE,"E62.0.2"),sQuery(id+"F6.wireOp",EDGE,"E62.0.3")])],"isStart":false});
            var Q28;
            Q28=makeQuery(id+"F7.opExtrude","CAP_FACE",FACE,{"disambiguationData":[OSD([sQuery(id+"F6.wireOp",EDGE,"E63.0.0"),sQuery(id+"F6.wireOp",EDGE,"E63.0.1"),sQuery(id+"F6.wireOp",EDGE,"E63.0.2"),sQuery(id+"F6.wireOp",EDGE,"E63.0.3")])],"isStart":false});
            var Q29;
            Q29=makeQuery(id+"F7.opExtrude","CAP_FACE",FACE,{"disambiguationData":[OSD([sQuery(id+"F6.wireOp",EDGE,"E64.0.0"),sQuery(id+"F6.wireOp",EDGE,"E64.0.1"),sQuery(id+"F6.wireOp",EDGE,"E64.0.2"),sQuery(id+"F6.wireOp",EDGE,"E64.0.3")])],"isStart":false});
            var Q30;
            Q30=makeQuery(id+"F7.opExtrude","CAP_FACE",FACE,{"disambiguationData":[OSD([sQuery(id+"F6.wireOp",EDGE,"E65.0.0"),sQuery(id+"F6.wireOp",EDGE,"E65.0.1"),sQuery(id+"F6.wireOp",EDGE,"E65.0.2"),sQuery(id+"F6.wireOp",EDGE,"E65.0.3")])],"isStart":false});
            var Q31;
            Q31=makeQuery(id+"F7.opExtrude","CAP_FACE",FACE,{"disambiguationData":[OSD([sQuery(id+"F6.wireOp",EDGE,"E66.0.0"),sQuery(id+"F6.wireOp",EDGE,"E66.0.1"),sQuery(id+"F6.wireOp",EDGE,"E66.0.2"),sQuery(id+"F6.wireOp",EDGE,"E66.0.3")])],"isStart":false});
            var Q32;
            Q32=makeQuery(id+"F7.opExtrude","CAP_FACE",FACE,{"disambiguationData":[OSD([sQuery(id+"F6.wireOp",EDGE,"E67.0.0"),sQuery(id+"F6.wireOp",EDGE,"E67.0.1"),sQuery(id+"F6.wireOp",EDGE,"E67.0.2"),sQuery(id+"F6.wireOp",EDGE,"E67.0.3")])],"isStart":false});
            var Q33;
            Q33=makeQuery(id+"F7.opExtrude","CAP_FACE",FACE,{"disambiguationData":[OSD([sQuery(id+"F6.wireOp",EDGE,"E68.0.0"),sQuery(id+"F6.wireOp",EDGE,"E68.0.1"),sQuery(id+"F6.wireOp",EDGE,"E68.0.2"),sQuery(id+"F6.wireOp",EDGE,"E68.0.3")])],"isStart":false});
            var Q34;
            Q34=makeQuery(id+"F7.opExtrude","CAP_FACE",FACE,{"disambiguationData":[OSD([sQuery(id+"F6.wireOp",EDGE,"E69.0.0"),sQuery(id+"F6.wireOp",EDGE,"E69.0.1"),sQuery(id+"F6.wireOp",EDGE,"E69.0.2"),sQuery(id+"F6.wireOp",EDGE,"E69.0.3")])],"isStart":false});
            var Q35;
            Q35=makeQuery(id+"F7.opExtrude","CAP_FACE",FACE,{"disambiguationData":[OSD([sQuery(id+"F6.wireOp",EDGE,"E70.0.0"),sQuery(id+"F6.wireOp",EDGE,"E70.0.1"),sQuery(id+"F6.wireOp",EDGE,"E70.0.2"),sQuery(id+"F6.wireOp",EDGE,"E70.0.3")])],"isStart":false});
            var Q36;
            Q36=makeQuery(id+"F7.opExtrude","CAP_FACE",FACE,{"disambiguationData":[OSD([sQuery(id+"F6.wireOp",EDGE,"E71.0.0"),sQuery(id+"F6.wireOp",EDGE,"E71.0.1"),sQuery(id+"F6.wireOp",EDGE,"E71.0.2"),sQuery(id+"F6.wireOp",EDGE,"E71.0.3")])],"isStart":false});
            var Q37;
            Q37=makeQuery(id+"F7.opExtrude","CAP_FACE",FACE,{"disambiguationData":[OSD([sQuery(id+"F6.wireOp",EDGE,"E72.0.0"),sQuery(id+"F6.wireOp",EDGE,"E72.0.1"),sQuery(id+"F6.wireOp",EDGE,"E72.0.2"),sQuery(id+"F6.wireOp",EDGE,"E72.0.3")])],"isStart":false});
            var Q38;
            Q38=makeQuery(id+"F7.opExtrude","CAP_FACE",FACE,{"disambiguationData":[OSD([sQuery(id+"F6.wireOp",EDGE,"E73.0.0"),sQuery(id+"F6.wireOp",EDGE,"E73.0.1"),sQuery(id+"F6.wireOp",EDGE,"E73.0.2"),sQuery(id+"F6.wireOp",EDGE,"E73.0.3")])],"isStart":false});
            var Q39;
            Q39=makeQuery(id+"F7.opExtrude","CAP_FACE",FACE,{"disambiguationData":[OSD([sQuery(id+"F6.wireOp",EDGE,"E74.0.0"),sQuery(id+"F6.wireOp",EDGE,"E74.0.1"),sQuery(id+"F6.wireOp",EDGE,"E74.0.2"),sQuery(id+"F6.wireOp",EDGE,"E74.0.3")])],"isStart":false});
            chamfer(context, id + "F8", {"entities" : qUnion([Q0, Q1, Q2, Q3, Q4, Q5, Q6, Q7, Q8, Q9, Q10, Q11, Q12, Q13, Q14, Q15, Q16, Q17, Q18, Q19, Q20, Q21, Q22, Q23, Q24, Q25, Q26, Q27, Q28, Q29, Q30, Q31, Q32, Q33, Q34, Q35, Q36, Q37, Q38, Q39]), "width" : 0.2 * mm, "tangentPropagation" : true});
        }
        {
            var Q0;
            Q0=makeQuery(id+"F1.opExtrude","CAP_FACE",FACE,{"disambiguationData":[OSD([sQuery(id+"F0.wireOp",EDGE,"E0.bottom"),sQuery(id+"F0.wireOp",EDGE,"E0.top"),sQuery(id+"F0.wireOp",EDGE,"E0.left"),sQuery(id+"F0.wireOp",EDGE,"E0.right")])],"isStart":false});
            var sketch = newSketch(context, id + "F9", { "sketchPlane" : qUnion([Q0])});
            skLineSegment(sketch, "E75.bottom", {"start": v(-13.3, 5.75) * mm, "end": v(-9.8, 5.75) * mm});
            skLineSegment(sketch, "E75.top", {"start": v(-13.3, -5.75) * mm, "end": v(-9.8, -5.75) * mm});
            skLineSegment(sketch, "E75.left", {"start": v(-13.3, 5.75) * mm, "end": v(-13.3, -5.75) * mm});
            skLineSegment(sketch, "E75.right", {"start": v(-9.8, 5.75) * mm, "end": v(-9.8, -5.75) * mm});
            skLineSegment(sketch, "E76", {"start": v(-9.8, 0) * mm, "end": v(0, 0) * mm, "construction": true});
            skSolve(sketch);
        }
        {
            var Q0;
            Q0 = qSketchRegion(id + "F9", true);
            extrude(context, id + "F10", {"entities" : qUnion([Q0]), "operationType" : NewBodyOperationType.ADD, "depth" : 2.3 * mm, "offsetDistance" : 25 * mm});
        }
        {
            var Q0;
            Q0=makeQuery(id+"F1.opExtrude","CAP_FACE",FACE,{"disambiguationData":[OSD([sQuery(id+"F0.wireOp",EDGE,"E0.bottom"),sQuery(id+"F0.wireOp",EDGE,"E0.top"),sQuery(id+"F0.wireOp",EDGE,"E0.left"),sQuery(id+"F0.wireOp",EDGE,"E0.right")])],"isStart":false});
            var sketch = newSketch(context, id + "F11", { "sketchPlane" : qUnion([Q0])});
            skLineSegment(sketch, "E77.bottom", {"start": v(-5.64, 2.31) * mm, "end": v(2.76, 2.31) * mm});
            skLineSegment(sketch, "E77.top", {"start": v(-5.64, -6.1) * mm, "end": v(2.76, -6.1) * mm});
            skLineSegment(sketch, "E77.left", {"start": v(-5.64, 2.31) * mm, "end": v(-5.64, -6.1) * mm});
            skLineSegment(sketch, "E77.right", {"start": v(2.76, 2.31) * mm, "end": v(2.76, -6.1) * mm});
            skLineSegment(sketch, "E78.bottom", {"start": v(5.24, 3.33) * mm, "end": v(10.75, 3.33) * mm});
            skLineSegment(sketch, "E78.top", {"start": v(5.24, -0.67) * mm, "end": v(10.75, -0.67) * mm});
            skLineSegment(sketch, "E78.left", {"start": v(5.24, 3.33) * mm, "end": v(5.24, -0.67) * mm});
            skLineSegment(sketch, "E78.right", {"start": v(10.75, 3.33) * mm, "end": v(10.75, -0.67) * mm});
            skSolve(sketch);
        }
        {
            var Q0;
            Q0 = qSketchRegion(id + "F11", true);
            extrude(context, id + "F12", {"entities" : qUnion([Q0]), "operationType" : NewBodyOperationType.ADD, "depth" : 1 * mm, "offsetDistance" : 25 * mm});
        }
    });
